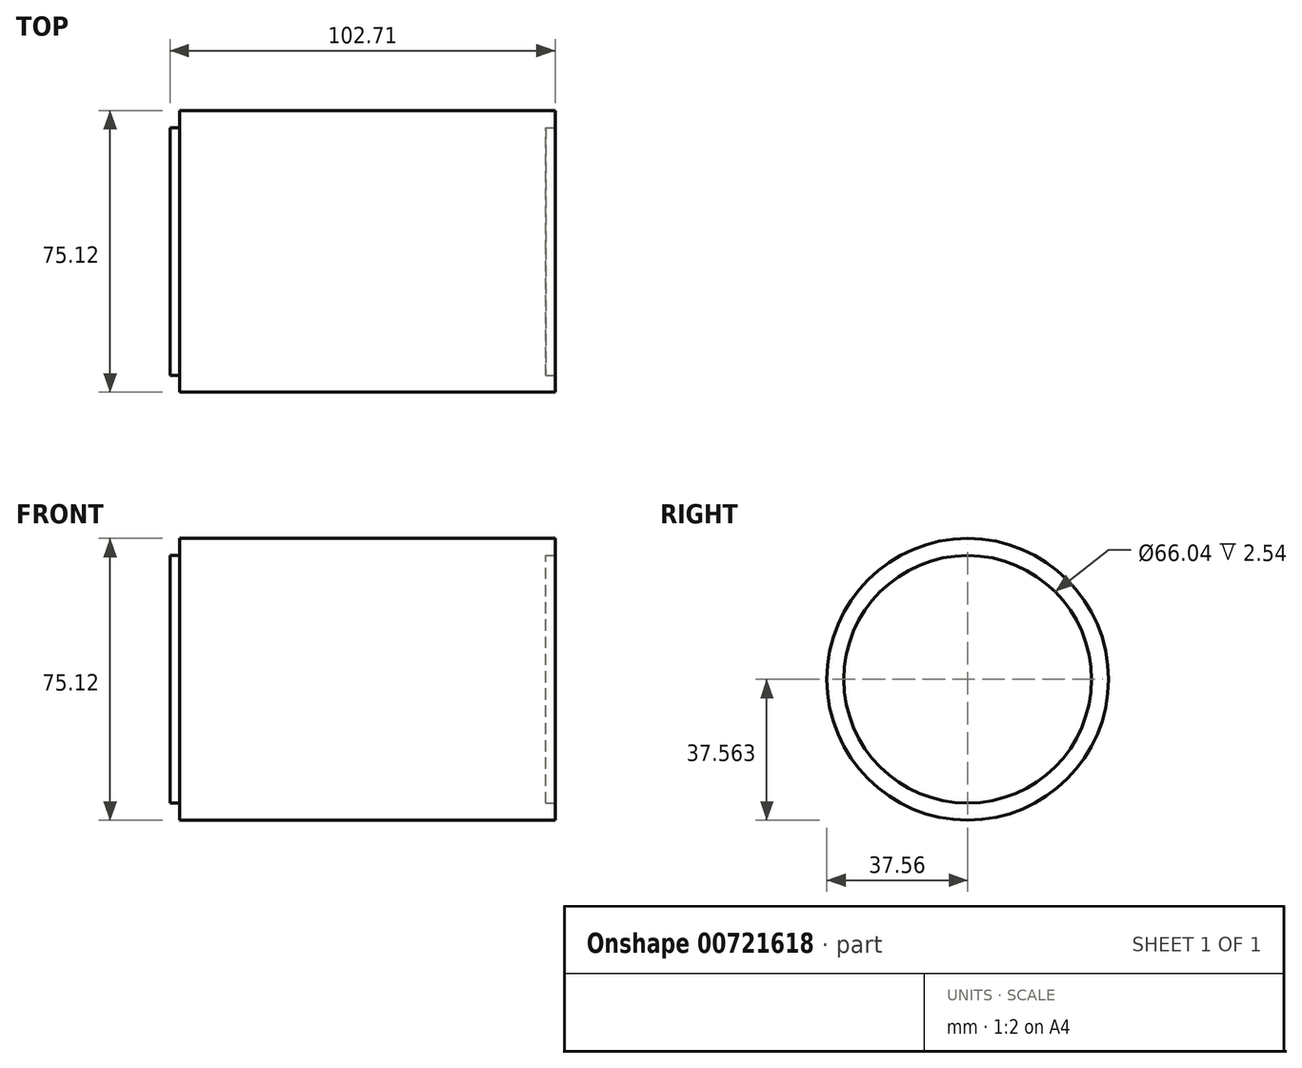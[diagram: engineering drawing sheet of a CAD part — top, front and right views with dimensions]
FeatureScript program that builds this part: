
annotation { "Feature Type Name" : "Feature", "Feature Type Description" : "" }
export const myFeature = defineFeature(function(context is Context, id is Id, definition is map)
    precondition{}
    {
        {
            var Q0;
            Q0=qCreatedBy(makeId("Front.planeOp"),FACE);
            var sketch = newSketch(context, id + "F0", { "sketchPlane" : qUnion([Q0])});
            skLineSegment(sketch, "E0.bottom", {"start": v(-53.29, 9.92) * mm, "end": v(46.88, 9.92) * mm});
            skLineSegment(sketch, "E0.top", {"start": v(-53.29, -27.64) * mm, "end": v(46.88, -27.64) * mm});
            skLineSegment(sketch, "E0.left", {"start": v(-53.29, 9.92) * mm, "end": v(-53.29, -27.64) * mm});
            skLineSegment(sketch, "E0.right", {"start": v(46.88, 9.92) * mm, "end": v(46.88, -27.64) * mm});
            skSolve(sketch);
        }
        {
            var Q0;
            Q0=makeQuery(id+"F0.imprint","IMPRINT",FACE,{"disambiguationData":[TD([[makeQuery(id+"F0.imprint","IMPRINT",EDGE,{"derivedFrom":sQuery(id+"F0.wireOp",EDGE,"E0.bottom")}),-1.0]])]});
            var Q1;
            Q1=sQuery(id+"F0.wireOp",EDGE,"E0.top");
            revolve(context, id + "F1", {"surfaceOperationType" : NewSurfaceOperationType.NEW, "entities" : qUnion([Q0]), "axis" : qUnion([Q1]), "revolveType" : RevolveType.FULL});
        }
        {
            var Q0;
            Q0=makeQuery(id+"F1.opRevolve","SWEPT_FACE",FACE,{"disambiguationData":[OSD([sQuery(id+"F0.wireOp",EDGE,"E0.left")])]});
            var sketch = newSketch(context, id + "F2", { "sketchPlane" : qUnion([Q0])});
            skCircle(sketch, "E1", {"center": v(0, -27.64) * mm, "radius": 33.02 * mm});
            skSolve(sketch);
        }
        {
            var Q0;
            Q0=makeQuery(id+"F1.opRevolve","SWEPT_FACE",FACE,{"disambiguationData":[OSD([sQuery(id+"F0.wireOp",EDGE,"E0.right")])]});
            var sketch = newSketch(context, id + "F3", { "sketchPlane" : qUnion([Q0])});
            skCircle(sketch, "E2", {"center": v(0, -27.64) * mm, "radius": 33.02 * mm});
            skSolve(sketch);
        }
        {
            var Q0;
            Q0=makeQuery(id+"F3.imprint","IMPRINT",FACE,{"disambiguationData":[TD([[makeQuery(id+"F3.imprint","IMPRINT",EDGE,{"derivedFrom":sQuery(id+"F3.wireOp",EDGE,"E2")}),1.0]])]});
            extrude(context, id + "F4", {"entities" : qUnion([Q0]), "operationType" : NewBodyOperationType.REMOVE, "oppositeDirection" : true, "depth" : 2.54 * mm, "offsetDistance" : 25.4 * mm});
        }
        {
            var Q0;
            Q0=makeQuery(id+"F2.imprint","IMPRINT",FACE,{"disambiguationData":[TD([[makeQuery(id+"F2.imprint","IMPRINT",EDGE,{"derivedFrom":sQuery(id+"F2.wireOp",EDGE,"E1")}),1.0]])]});
            extrude(context, id + "F5", {"entities" : qUnion([Q0]), "operationType" : NewBodyOperationType.ADD, "depth" : 2.54 * mm, "offsetDistance" : 25.4 * mm});
        }
    });
